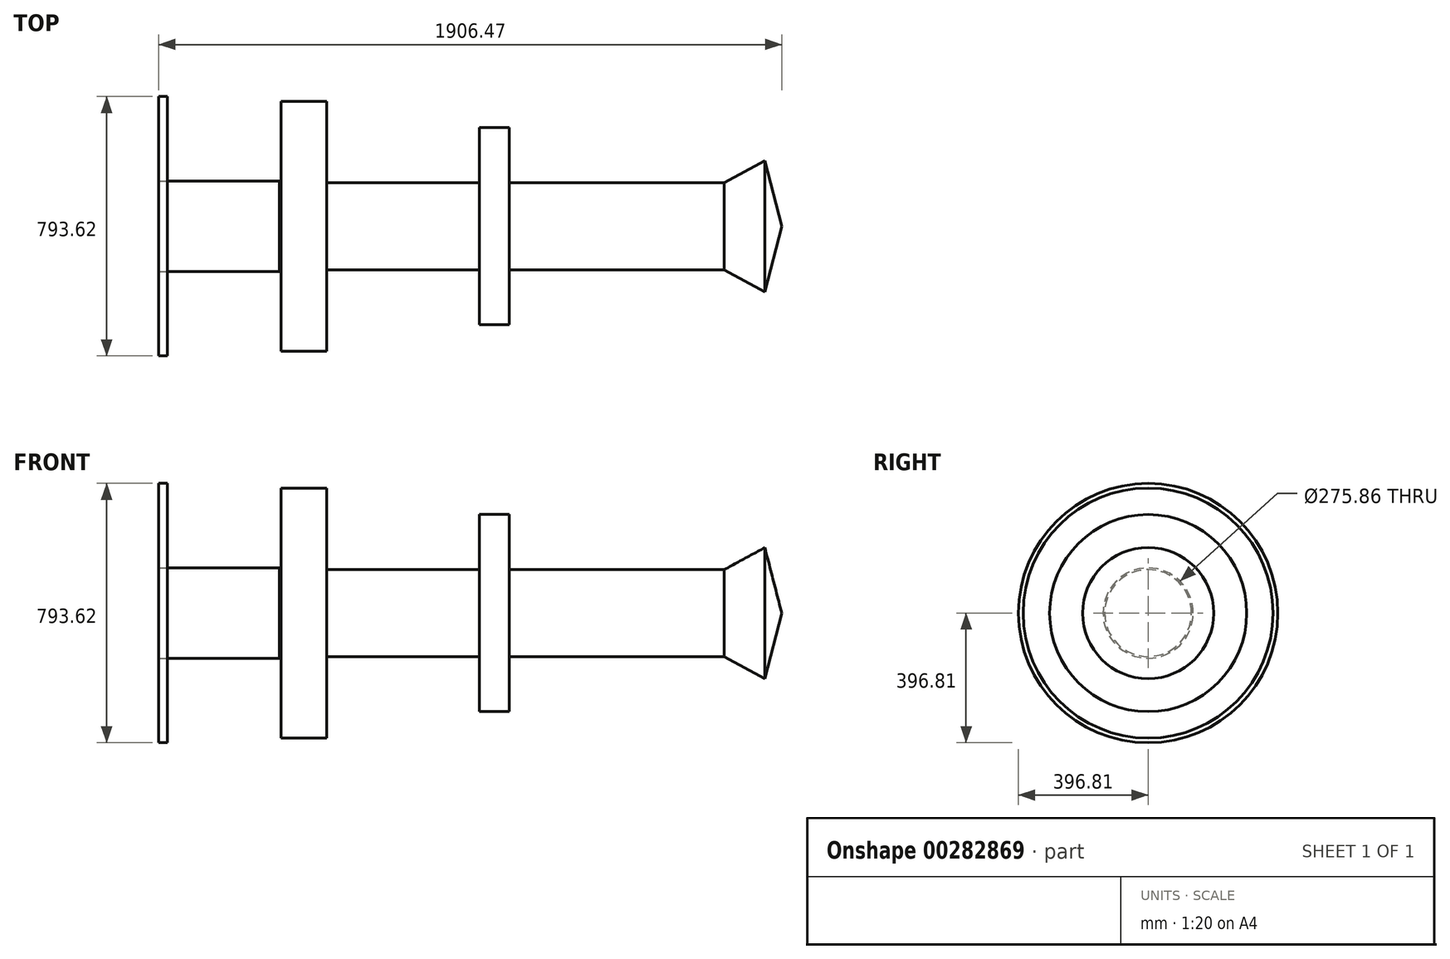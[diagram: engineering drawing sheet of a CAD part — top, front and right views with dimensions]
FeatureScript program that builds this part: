
annotation { "Feature Type Name" : "Feature", "Feature Type Description" : "" }
export const myFeature = defineFeature(function(context is Context, id is Id, definition is map)
    precondition{}
    {
        {
            var Q0;
            Q0=qCreatedBy(makeId("Front.planeOp"),FACE);
            var sketch = newSketch(context, id + "F0", { "sketchPlane" : qUnion([Q0])});
            skLineSegment(sketch, "E0", {"start": v(-607.98, 0) * mm, "end": v(-607.98, 382.55) * mm});
            skLineSegment(sketch, "E1", {"start": v(-607.98, 382.55) * mm, "end": v(-467.33, 382.55) * mm});
            skLineSegment(sketch, "E2", {"start": v(-467.33, 382.55) * mm, "end": v(-467.33, 132.9) * mm});
            skLineSegment(sketch, "E3", {"start": v(-467.33, 132.9) * mm, "end": v(0, 132.9) * mm});
            skLineSegment(sketch, "E4", {"start": v(0, 132.9) * mm, "end": v(0, 301.67) * mm});
            skLineSegment(sketch, "E5", {"start": v(0, 301.67) * mm, "end": v(91.76, 301.67) * mm});
            skLineSegment(sketch, "E6", {"start": v(91.76, 301.67) * mm, "end": v(91.76, 132.9) * mm});
            skLineSegment(sketch, "E7", {"start": v(91.76, 132.9) * mm, "end": v(749.3, 132.9) * mm});
            skLineSegment(sketch, "E8", {"start": v(-607.98, 0) * mm, "end": v(925.1, 0) * mm});
            skLineSegment(sketch, "E9", {"start": v(925.1, 0) * mm, "end": v(873.5, 200.67) * mm});
            skLineSegment(sketch, "E10", {"start": v(873.5, 200.67) * mm, "end": v(749.3, 132.9) * mm});
            skSolve(sketch);
        }
        {
            var Q0;
            Q0=makeQuery(id+"F0.imprint","IMPRINT",FACE,{"disambiguationData":[TD([[makeQuery(id+"F0.imprint","IMPRINT",EDGE,{"derivedFrom":sQuery(id+"F0.wireOp",EDGE,"E0")}),-1.0]])]});
            var Q1;
            Q1=sQuery(id+"F0.wireOp",EDGE,"E8");
            revolve(context, id + "F1", {"entities" : qUnion([Q0]), "axis" : qUnion([Q1]), "revolveType" : RevolveType.FULL});
        }
        {
            var Q0;
            Q0=makeQuery(id+"F1.opRevolve","SWEPT_FACE",FACE,{"disambiguationData":[OSD([sQuery(id+"F0.wireOp",EDGE,"E0")])]});
            var sketch = newSketch(context, id + "F2", { "sketchPlane" : qUnion([Q0])});
            skCircle(sketch, "E11", {"center": v(0, 0) * mm, "radius": 137.93 * mm});
            skSolve(sketch);
        }
        {
            var Q0;
            Q0=makeQuery(id+"F2.imprint","IMPRINT",FACE,{"disambiguationData":[TD([[makeQuery(id+"F2.imprint","IMPRINT",EDGE,{"derivedFrom":sQuery(id+"F2.wireOp",EDGE,"E11")}),1.0]])]});
            extrude(context, id + "F3", {"entities" : qUnion([Q0]), "depth" : 347.98 * mm, "hasSecondDirection" : true, "secondDirectionOppositeDirection" : false, "secondDirectionDepth" : 5.08 * mm});
        }
        {
            var Q0;
            Q0=makeQuery(id+"F3.opExtrude","CAP_FACE",FACE,{"disambiguationData":[OSD([sQuery(id+"F2.wireOp",EDGE,"E11")])],"isStart":false});
            var sketch = newSketch(context, id + "F4", { "sketchPlane" : qUnion([Q0])});
            skCircle(sketch, "E12", {"center": v(0, 0) * mm, "radius": 396.8 * mm});
            skSolve(sketch);
        }
        {
            var Q0;
            Q0=makeQuery(id+"F4.imprint","IMPRINT",FACE,{"disambiguationData":[TD([[makeQuery(id+"F4.imprint","IMPRINT",EDGE,{"derivedFrom":sQuery(id+"F4.wireOp",EDGE,"E12")}),1.0]])]});
            extrude(context, id + "F5", {"entities" : qUnion([Q0]), "depth" : 25.4 * mm});
        }
    });
